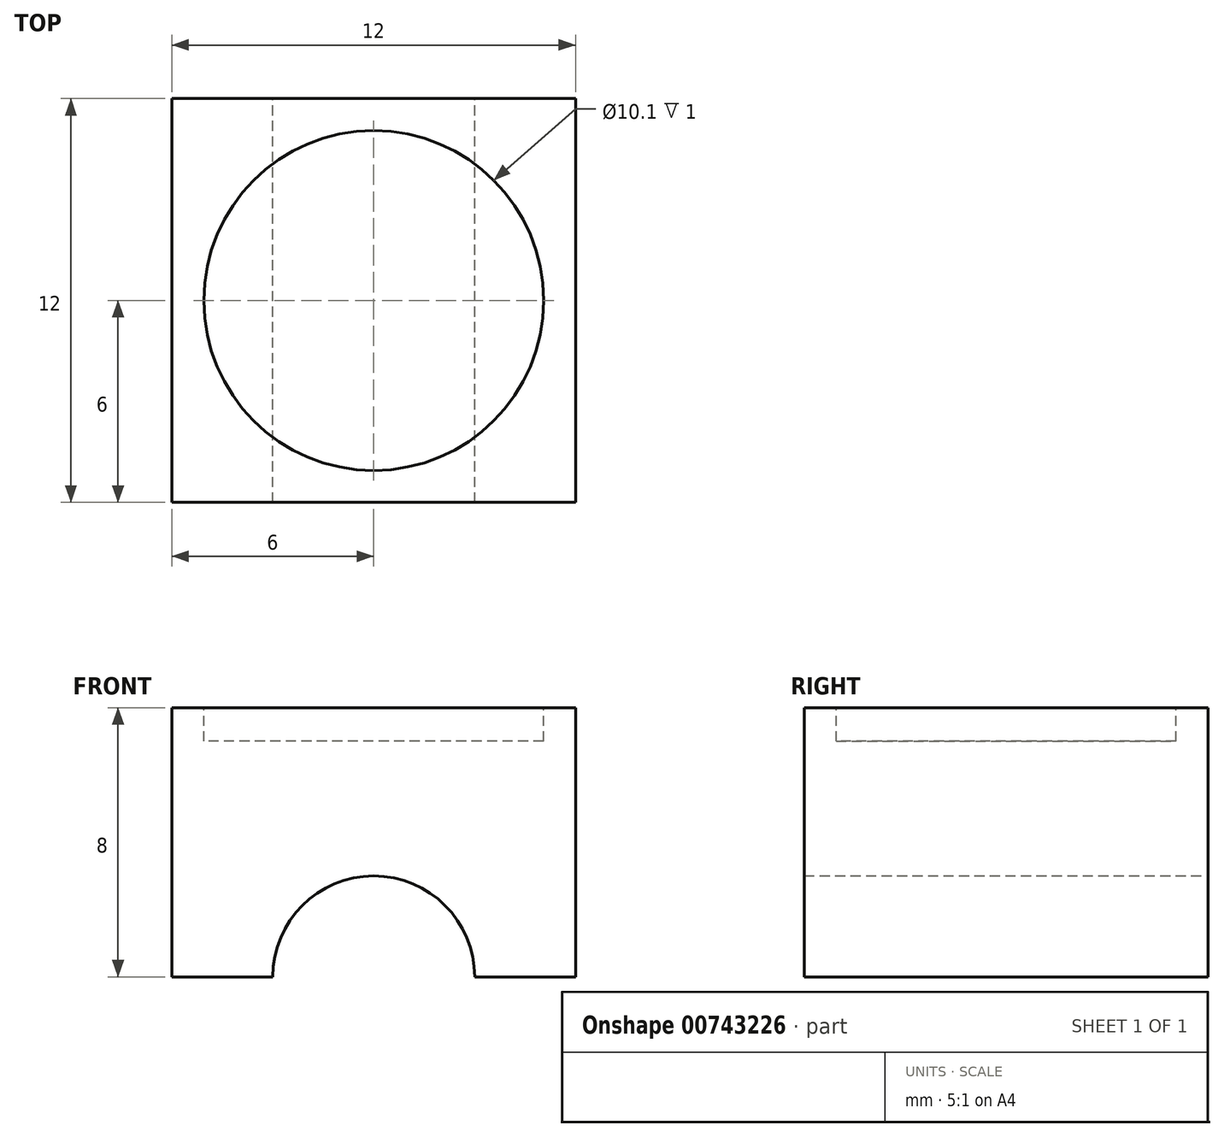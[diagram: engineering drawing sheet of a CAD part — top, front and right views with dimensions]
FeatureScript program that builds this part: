
annotation { "Feature Type Name" : "Feature", "Feature Type Description" : "" }
export const myFeature = defineFeature(function(context is Context, id is Id, definition is map)
    precondition{}
    {
        {
            var Q0;
            Q0=qCreatedBy(makeId("Front.planeOp"),FACE);
            var sketch = newSketch(context, id + "F0", { "sketchPlane" : qUnion([Q0])});
            skLineSegment(sketch, "E0.bottom", {"start": v(-6, 4) * mm, "end": v(6, 4) * mm});
            skLineSegment(sketch, "E0.left", {"start": v(-6, 4) * mm, "end": v(-6, -4) * mm});
            skLineSegment(sketch, "E0.right", {"start": v(6, 4) * mm, "end": v(6, -4) * mm});
            skPoint(sketch, "E0.middle", {"position": v(0, 0) * mm});
            skLineSegment(sketch, "E1", {"start": v(-6, -4) * mm, "end": v(-3, -4) * mm});
            skLineSegment(sketch, "E2", {"start": v(6, -4) * mm, "end": v(3, -4) * mm});
            skArc(sketch, "E3", {"start": v(3, -4) * mm, "mid": v(0, -1) * mm, "end": v(-3, -4) * mm});
            skLineSegment(sketch, "E4", {"start": v(0, 5.5) * mm, "end": v(0, -7.3) * mm, "construction": true});
            skSolve(sketch);
        }
        {
            var Q0;
            Q0=makeQuery(id+"F0.imprint","IMPRINT",FACE,{"disambiguationData":[TD([[makeQuery(id+"F0.imprint","IMPRINT",EDGE,{"derivedFrom":sQuery(id+"F0.wireOp",EDGE,"E0.bottom")}),-1.0]])]});
            extrude(context, id + "F1", {"entities" : qUnion([Q0]), "depth" : 12 * mm, "offsetDistance" : 25 * mm});
        }
        {
            var Q0;
            Q0=makeQuery(id+"F1.opExtrude","SWEPT_FACE",FACE,{"disambiguationData":[OSD([sQuery(id+"F0.wireOp",EDGE,"E0.bottom")])]});
            var sketch = newSketch(context, id + "F2", { "sketchPlane" : qUnion([Q0])});
            skCircle(sketch, "E5", {"center": v(0, -6) * mm, "radius": 5.05 * mm});
            skPoint(sketch, "E5.centerSnap0", {"position": v(-6, -6) * mm});
            skSolve(sketch);
        }
        {
            var Q0;
            Q0=makeQuery(id+"F2.imprint","IMPRINT",FACE,{"disambiguationData":[TD([[makeQuery(id+"F2.imprint","IMPRINT",EDGE,{"derivedFrom":sQuery(id+"F2.wireOp",EDGE,"E5")}),1.0]])]});
            extrude(context, id + "F3", {"entities" : qUnion([Q0]), "operationType" : NewBodyOperationType.REMOVE, "oppositeDirection" : true, "depth" : 1 * mm, "offsetDistance" : 25 * mm});
        }
    });
